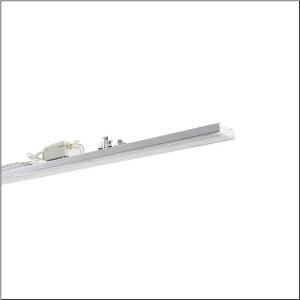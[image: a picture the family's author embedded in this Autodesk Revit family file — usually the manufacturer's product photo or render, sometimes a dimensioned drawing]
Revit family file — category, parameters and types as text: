
# Revit family: licross_r__21_recessed_ho_52tl1ecn4cxs_20c2
name_source: partatom
category: Lighting Fixtures
units: mm (PartAtom-declared; Revit-internal decimal feet)

## family parameters
Cut with Voids When Loaded = No
Host = Face
Light Source = No
Part Type = Normal
Room Calculation Point = No
Round Connector Dimension = Use Diameter
Shared = No

## types (1)
- --- (1 x LED, 12350 lm, 68.4 W, 4000K)
    Apparent Load = 68 VA
    CIE Flux Codes = 85 95 99 100 100
    Color Rendering = 80
    Color Temperature = 4000K
    Default Elevation = 1800 mm
    Description = Licross® 21 Recessed HO, luminaire insert, of sheet steel, galvanised, coil coated, white, length: 1.500mm, width: 66mm, height: 67mm, LED rated luminous flux: 12.350lm, light colour: 840, control gear: ON/OFF Multilumen, CLOi, control gear: ECG Multilumen, with plug, 3-pole, with phase selection, mains connection: 220..240V, AC, 50/60Hz, start of lifetime: 69W, end of service life: 83W, halogen-free wiring, primary light control with lens, of plastic, primary optical cover: cover, of PMMA, light emission: direct distribution, primary light characteristic: symmetric, protection rating (complete): IP40, insulation class (complete): insulation class I (protective earthing), certification: CE, ENEC, VDE, UKCA, protection symbol: D if used in an environment without relevant dust loads with corresponding accessories, impact resistance: IK06, permissible ambient temperature for indoor applications: -35..+30°C, corresponds to IFS (International Featured Standards) requirements for safety and quality in the food industry, reducing of maximum allowable ambient temperature of 5°C with ceiling mounting, LABS conformity tested according to VDMA 24364:2018-05, packaging unit: 1 piece
    Height = 58 mm
    Lamp = 1 x LED
    Lamp Light Flux = 12350 lm
    Lamp Power = 68.4 W
    Lamp count = 1
    Length = 1500 mm
    Luminous efficacy = 181 lm/W
    Manufacturer = Siteco
    ModVariant = No
    Model = 52TL1ECN4CXS
    Mounting Place = Ceiling
    Mounting Type = Pendant
    Number of Poles = 1
    OnlyDefault = Yes
    Power Factor = 1
    Product Name = Licross® 21 Recessed HO
    Product group = luminaire insert
    ProductGroupID = 901
    Protection Class = Protection class I
    Protection Degree = IP 40
    RLX_Detail_Level = 1
    RLX_Emergency_Light_Flux = 0 lm
    RLX_Emergency_Type = 0
    RLX_Emergency_Type_DB = No
    RlxData = <blob elided: 22453 chars, md5=2d2cbd3c>
    Socket = socket
    Standby Power = 0 W
    System Light Flux = 12350 lm
    System Power = 68 W
    Type Comments = factory setting: luminous flux: 100 % | (A | C | E) | 161 mA
    Type Image = l_1296930.jpg
    URL = http://relux.com
    VarID = @adj_040065
    Voltage = 0 V
    Weight = 0.00 kg
    Width = 66 mm

## geometry (parser evidence)
native form markers: Blend x4, Sweep x13
no freeform markers — native parametric forms only
